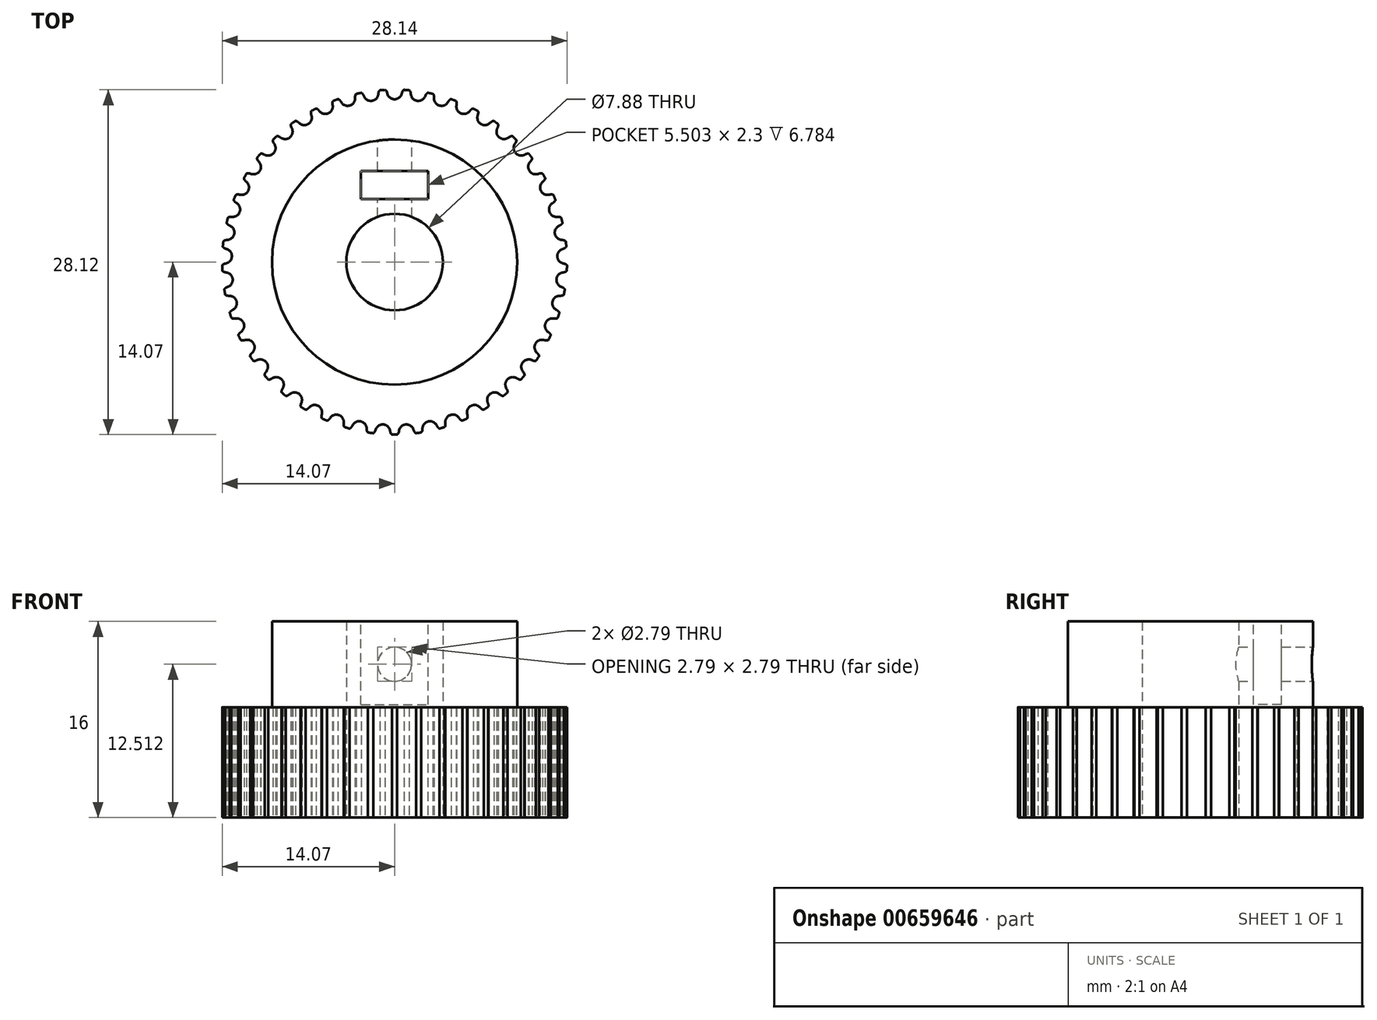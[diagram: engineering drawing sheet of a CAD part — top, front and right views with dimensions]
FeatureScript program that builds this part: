
annotation { "Feature Type Name" : "Feature", "Feature Type Description" : "" }
export const myFeature = defineFeature(function(context is Context, id is Id, definition is map)
    precondition{}
    {
        {
            assignVariable(context, id + "F0", {"name" : "Teeth", "anyValue" : 45});
        }
        {
            var Q0;
            Q0=qCreatedBy(makeId("Top.planeOp"),FACE);
            var sketch = newSketch(context, id + "F1", { "sketchPlane" : qUnion([Q0])});
            skCircle(sketch, "E0", {"center": v(0, 0) * mm, "radius": 14.07 * mm});
            skSolve(sketch);
        }
        {
            var Q0;
            Q0=qCreatedBy(makeId("Top.planeOp"),FACE);
            var sketch = newSketch(context, id + "F2", { "sketchPlane" : qUnion([Q0])});
            skArc(sketch, "E1.0", {"start": v(0.77, 14.05) * mm, "mid": v(0, 14.07) * mm, "end": v(-0.77, 14.05) * mm});
            skLineSegment(sketch, "E2", {"start": v(0, 0) * mm, "end": v(0, 13.9) * mm, "construction": true});
            skArc(sketch, "E3", {"start": v(0, 13.28) * mm, "mid": v(-0.38, 13.42) * mm, "end": v(-0.6, 13.76) * mm});
            skArc(sketch, "E4", {"start": v(-0.6, 13.76) * mm, "mid": v(-0.63, 13.87) * mm, "end": v(-0.68, 13.96) * mm});
            skArc(sketch, "E5", {"start": v(-0.68, 13.96) * mm, "mid": v(-0.71, 14.01) * mm, "end": v(-0.77, 14.05) * mm});
            skArc(sketch, "E6.MirrorCS", {"start": v(0, 13.28) * mm, "mid": v(0.38, 13.42) * mm, "end": v(0.6, 13.76) * mm});
            skArc(sketch, "E7.MirrorCS", {"start": v(0.68, 13.96) * mm, "mid": v(0.71, 14.01) * mm, "end": v(0.77, 14.05) * mm});
            skArc(sketch, "E8.MirrorCS", {"start": v(0.6, 13.76) * mm, "mid": v(0.63, 13.87) * mm, "end": v(0.68, 13.96) * mm});
            skSolve(sketch);
        }
        {
            var Q0;
            Q0=qSketchRegion(id+"F1",true);
            extrude(context, id + "F3", {"entities" : qUnion([Q0]), "depth" : 9 * mm, "offsetDistance" : 25 * mm});
        }
        {
            var Q0;
            Q0=makeQuery(id+"F2.imprint","IMPRINT",FACE,{"disambiguationData":[TD([[makeQuery(id+"F2.imprint","IMPRINT",EDGE,{"derivedFrom":sQuery(id+"F2.wireOp",EDGE,"E1.0")}),1.0]])]});
            extrude(context, id + "F4", {"entities" : qUnion([Q0]), "depth" : 25 * mm, "offsetDistance" : 25 * mm});
        }
        {
            var Q0;
            Q0=makeQuery(id+"F4.opExtrude","SWEPT_BODY",BODY,{"disambiguationData":[OSD([sQuery(id+"F2.wireOp",EDGE,"E1.0"),sQuery(id+"F2.wireOp",EDGE,"E3"),sQuery(id+"F2.wireOp",EDGE,"E4"),sQuery(id+"F2.wireOp",EDGE,"E5"),sQuery(id+"F2.wireOp",EDGE,"E6.MirrorCS"),sQuery(id+"F2.wireOp",EDGE,"E7.MirrorCS"),sQuery(id+"F2.wireOp",EDGE,"E8.MirrorCS")])]});
            var Q1;
            Q1=sQuery(id+"F1.wireOp",EDGE,"E0");
            circularPattern(context, id + "F5", {"operationType" : NewBodyOperationType.REMOVE, "entities" : qUnion([Q0]), "axis" : qUnion([Q1]), "angle" : 360 * degree, "instanceCount" : getVariable(context, 'Teeth'), "equalSpace" : true});
        }
        {
            var Q0;
            Q0=makeQuery(id+"F3.opExtrude","CAP_FACE",FACE,{"disambiguationData":[OSD([sQuery(id+"F1.wireOp",EDGE,"E0")])],"isStart":false});
            var sketch = newSketch(context, id + "F6", { "sketchPlane" : qUnion([Q0])});
            skCircle(sketch, "E9", {"center": v(0, 0) * mm, "radius": 10 * mm});
            skSolve(sketch);
        }
        {
            var Q0;
            Q0 = qSketchRegion(id + "F6", true);
            extrude(context, id + "F7", {"entities" : qUnion([Q0]), "operationType" : NewBodyOperationType.ADD, "depth" : 7 * mm, "offsetDistance" : 25 * mm});
        }
        {
            var Q0;
            Q0=qCreatedBy(makeId("Top.planeOp"),FACE);
            var sketch = newSketch(context, id + "F8", { "sketchPlane" : qUnion([Q0])});
            skCircle(sketch, "E10", {"center": v(0, 0) * mm, "radius": 3.94 * mm});
            skSolve(sketch);
        }
        {
            var Q0;
            Q0=qSketchRegion(id+"F8",true);
            var Q1;
            Q1=sQuery(id+"F8.wireOp",EDGE,"E10");
            extrude(context, id + "F9", {"entities" : qUnion([Q0]), "operationType" : NewBodyOperationType.REMOVE, "surfaceEntities" : qUnion([Q1]), "endBound" : BoundingType.THROUGH_ALL, "depth" : 25 * mm, "offsetDistance" : 25 * mm});
        }
        {
            var Q0;
            Q0=makeQuery(id+"F7.opExtrude","CAP_FACE",FACE,{"disambiguationData":[OSD([sQuery(id+"F6.wireOp",EDGE,"E9")])],"isStart":false});
            var sketch = newSketch(context, id + "F10", { "sketchPlane" : qUnion([Q0])});
            skLineSegment(sketch, "E11", {"start": v(0, 10) * mm, "end": v(0, 7.44) * mm, "construction": true});
            skLineSegment(sketch, "E12.bottom", {"start": v(-2.75, 7.44) * mm, "end": v(2.75, 7.44) * mm});
            skLineSegment(sketch, "E12.top", {"start": v(-2.75, 7.44) * mm, "end": v(2.75, 7.44) * mm});
            skLineSegment(sketch, "E12.left", {"start": v(-2.75, 7.44) * mm, "end": v(-2.75, 7.44) * mm});
            skLineSegment(sketch, "E12.right", {"start": v(2.75, 7.44) * mm, "end": v(2.75, 7.44) * mm});
            skPoint(sketch, "E12.middle", {"position": v(0, 7.44) * mm});
            skLineSegment(sketch, "E13.top", {"start": v(-2.75, 5.14) * mm, "end": v(2.75, 5.14) * mm});
            skLineSegment(sketch, "E13.left", {"start": v(-2.75, 7.44) * mm, "end": v(-2.75, 5.14) * mm});
            skLineSegment(sketch, "E13.right", {"start": v(2.75, 7.44) * mm, "end": v(2.75, 5.14) * mm});
            skSolve(sketch);
        }
        {
            var Q0;
            Q0 = qSketchRegion(id + "F10", true);
            extrude(context, id + "F11", {"entities" : qUnion([Q0]), "operationType" : NewBodyOperationType.REMOVE, "oppositeDirection" : true, "depth" : 6.78 * mm, "offsetDistance" : 25 * mm});
        }
        {
            var Q0;
            Q0=makeQuery(id+"F11.boolean.opBoolean","COPY",FACE,{"derivedFrom":makeQuery(id+"F11.opExtrude","SWEPT_FACE",FACE,{"disambiguationData":[OSD([sQuery(id+"F10.wireOp",EDGE,"E13.top")])]})});
            var sketch = newSketch(context, id + "F12", { "sketchPlane" : qUnion([Q0])});
            skLineSegment(sketch, "E14", {"start": v(0, 16) * mm, "end": v(0, 13.9) * mm, "construction": true});
            skLineSegment(sketch, "E15", {"start": v(0, 13.9) * mm, "end": v(0, 11.12) * mm, "construction": true});
            skCircle(sketch, "E16", {"center": v(0, 12.51) * mm, "radius": 1.4 * mm});
            skSolve(sketch);
        }
        {
            var Q0;
            Q0=makeQuery(id+"F12.imprint","IMPRINT",FACE,{"disambiguationData":[TD([[makeQuery(id+"F12.imprint","IMPRINT",EDGE,{"derivedFrom":sQuery(id+"F12.wireOp",EDGE,"E16")}),1.0]])]});
            extrude(context, id + "F13", {"entities" : qUnion([Q0]), "operationType" : NewBodyOperationType.REMOVE, "oppositeDirection" : true, "depth" : 5 * mm, "offsetDistance" : 25 * mm, "hasSecondDirection" : true, "secondDirectionOppositeDirection" : false, "secondDirectionDepth" : 15 * mm});
        }
    });
